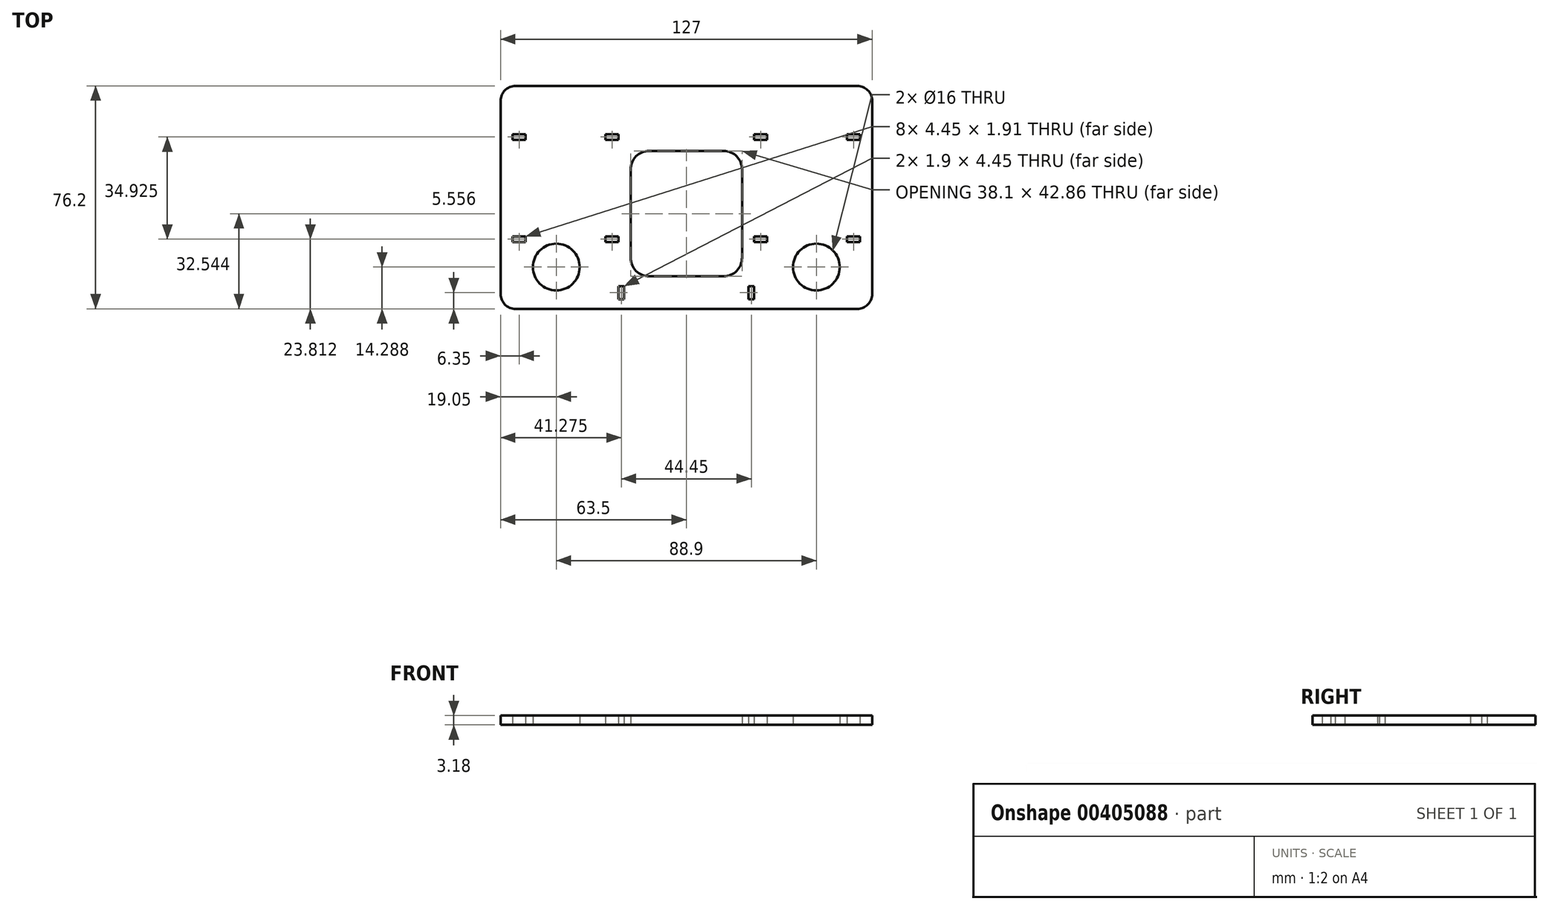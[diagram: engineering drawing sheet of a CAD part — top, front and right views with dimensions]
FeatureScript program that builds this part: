
annotation { "Feature Type Name" : "Feature", "Feature Type Description" : "" }
export const myFeature = defineFeature(function(context is Context, id is Id, definition is map)
    precondition{}
    {
        {
            var Q0;
            Q0=qCreatedBy(makeId("Top.planeOp"),FACE);
            var sketch = newSketch(context, id + "F0", { "sketchPlane" : qUnion([Q0])});
            skLineSegment(sketch, "E0.bottom", {"start": v(63.5, 31.75) * mm, "end": v(-63.5, 31.75) * mm, "construction": true});
            skLineSegment(sketch, "E0.top", {"start": v(63.5, -31.75) * mm, "end": v(-63.5, -31.75) * mm});
            skLineSegment(sketch, "E0.left", {"start": v(63.5, 31.75) * mm, "end": v(63.5, -31.75) * mm});
            skLineSegment(sketch, "E0.right", {"start": v(-63.5, 31.75) * mm, "end": v(-63.5, -31.75) * mm});
            skLineSegment(sketch, "E1.bottom", {"start": v(-19.05, 22.23) * mm, "end": v(19.05, 22.23) * mm});
            skLineSegment(sketch, "E1.top", {"start": v(-19.05, -20.64) * mm, "end": v(19.05, -20.64) * mm});
            skLineSegment(sketch, "E1.left", {"start": v(-19.05, 22.23) * mm, "end": v(-19.05, -20.64) * mm});
            skLineSegment(sketch, "E1.right", {"start": v(19.05, 22.23) * mm, "end": v(19.05, -20.64) * mm});
            skPoint(sketch, "E1.middle", {"position": v(0, 0.8) * mm});
            skLineSegment(sketch, "E2", {"start": v(-63.5, 0) * mm, "end": v(0, 0) * mm, "construction": true});
            skLineSegment(sketch, "E3", {"start": v(0, 0) * mm, "end": v(0, 31.75) * mm, "construction": true});
            skCircle(sketch, "E4", {"center": v(44.45, -17.46) * mm, "radius": 8 * mm});
            skLineSegment(sketch, "E5", {"start": v(19.05, -3.17) * mm, "end": v(63.5, -3.17) * mm, "construction": true});
            skLineSegment(sketch, "E6", {"start": v(44.45, -3.17) * mm, "end": v(44.45, -31.75) * mm, "construction": true});
            skCircle(sketch, "E7.MirrorC", {"center": v(-44.45, -17.46) * mm, "radius": 8 * mm});
            skLineSegment(sketch, "E8.bottom", {"start": v(-59.37, 27.94) * mm, "end": v(-54.93, 27.94) * mm});
            skLineSegment(sketch, "E8.top", {"start": v(-59.37, 26.04) * mm, "end": v(-54.93, 26.04) * mm});
            skLineSegment(sketch, "E8.left", {"start": v(-59.37, 27.94) * mm, "end": v(-59.37, 26.04) * mm});
            skLineSegment(sketch, "E8.right", {"start": v(-54.93, 27.94) * mm, "end": v(-54.93, 26.04) * mm});
            skPoint(sketch, "E8.middle", {"position": v(-57.15, 26.99) * mm});
            skArc(sketch, "E9", {"start": v(-57.15, 31.75) * mm, "mid": v(-61.64, 29.9) * mm, "end": v(-63.5, 25.4) * mm, "construction": true});
            skLineSegment(sketch, "E10.1.0.0", {"start": v(-27.62, 27.94) * mm, "end": v(-23.18, 27.94) * mm});
            skLineSegment(sketch, "E10.1.0.1", {"start": v(-27.62, 27.94) * mm, "end": v(-27.62, 26.04) * mm});
            skLineSegment(sketch, "E10.1.0.2", {"start": v(-27.62, 26.04) * mm, "end": v(-23.18, 26.04) * mm});
            skLineSegment(sketch, "E10.1.0.3", {"start": v(-23.18, 27.94) * mm, "end": v(-23.18, 26.04) * mm});
            skLineSegment(sketch, "E10.direction1", {"start": v(-59.37, 27.94) * mm, "end": v(-27.62, 27.94) * mm, "construction": true});
            skLineSegment(sketch, "E11", {"start": v(-63.5, 9.53) * mm, "end": v(-19.05, 9.53) * mm, "construction": true});
            skLineSegment(sketch, "E12.MirrorCS", {"start": v(-59.37, -6.99) * mm, "end": v(-54.93, -6.99) * mm});
            skLineSegment(sketch, "E13.MirrorCS", {"start": v(-54.93, -8.89) * mm, "end": v(-54.93, -6.99) * mm});
            skLineSegment(sketch, "E14.MirrorCS", {"start": v(-59.37, -8.89) * mm, "end": v(-54.93, -8.89) * mm});
            skPoint(sketch, "E15.MirrorP", {"position": v(-57.15, -7.94) * mm});
            skLineSegment(sketch, "E16.MirrorCS", {"start": v(-59.37, -8.89) * mm, "end": v(-59.37, -6.99) * mm});
            skLineSegment(sketch, "E17.MirrorCS", {"start": v(-27.62, -8.89) * mm, "end": v(-23.18, -8.89) * mm});
            skLineSegment(sketch, "E18.MirrorCS", {"start": v(-27.62, -6.99) * mm, "end": v(-23.18, -6.99) * mm});
            skLineSegment(sketch, "E19.MirrorCS", {"start": v(-27.62, -8.89) * mm, "end": v(-27.62, -6.99) * mm});
            skLineSegment(sketch, "E20.MirrorCS", {"start": v(-23.18, -8.89) * mm, "end": v(-23.18, -6.99) * mm});
            skLineSegment(sketch, "E21.MirrorCS", {"start": v(59.37, 27.94) * mm, "end": v(54.93, 27.94) * mm});
            skLineSegment(sketch, "E22.MirrorCS", {"start": v(59.37, 27.94) * mm, "end": v(59.37, 26.04) * mm});
            skLineSegment(sketch, "E23.MirrorCS", {"start": v(59.37, 26.04) * mm, "end": v(54.93, 26.04) * mm});
            skLineSegment(sketch, "E24.MirrorCS", {"start": v(54.93, 27.94) * mm, "end": v(54.93, 26.04) * mm});
            skLineSegment(sketch, "E25.MirrorCS", {"start": v(27.62, 26.04) * mm, "end": v(23.18, 26.04) * mm});
            skLineSegment(sketch, "E26.MirrorCS", {"start": v(27.62, 27.94) * mm, "end": v(27.62, 26.04) * mm});
            skLineSegment(sketch, "E27.MirrorCS", {"start": v(23.18, 27.94) * mm, "end": v(23.18, 26.04) * mm});
            skLineSegment(sketch, "E28.MirrorCS", {"start": v(27.62, 27.94) * mm, "end": v(23.18, 27.94) * mm});
            skLineSegment(sketch, "E29.MirrorCS", {"start": v(59.37, -8.89) * mm, "end": v(59.37, -6.99) * mm});
            skLineSegment(sketch, "E30.MirrorCS", {"start": v(59.37, -6.98) * mm, "end": v(54.93, -6.98) * mm});
            skLineSegment(sketch, "E31.MirrorCS", {"start": v(54.93, -8.89) * mm, "end": v(54.93, -6.99) * mm});
            skLineSegment(sketch, "E32.MirrorCS", {"start": v(59.37, -8.89) * mm, "end": v(54.93, -8.89) * mm});
            skLineSegment(sketch, "E33.MirrorCS", {"start": v(27.62, -6.98) * mm, "end": v(23.18, -6.98) * mm});
            skLineSegment(sketch, "E34.MirrorCS", {"start": v(27.62, -8.89) * mm, "end": v(23.18, -8.89) * mm});
            skLineSegment(sketch, "E35.MirrorCS", {"start": v(27.62, -8.89) * mm, "end": v(27.62, -6.99) * mm});
            skLineSegment(sketch, "E36.MirrorCS", {"start": v(23.18, -8.89) * mm, "end": v(23.18, -6.99) * mm});
            skLineSegment(sketch, "E37.bottom", {"start": v(-21.27, -28.42) * mm, "end": v(-23.18, -28.42) * mm});
            skLineSegment(sketch, "E37.top", {"start": v(-21.27, -23.97) * mm, "end": v(-23.18, -23.97) * mm});
            skLineSegment(sketch, "E37.left", {"start": v(-21.27, -28.42) * mm, "end": v(-21.27, -23.97) * mm});
            skLineSegment(sketch, "E37.right", {"start": v(-23.18, -28.42) * mm, "end": v(-23.18, -23.97) * mm});
            skPoint(sketch, "E37.middle", {"position": v(-22.23, -26.2) * mm});
            skLineSegment(sketch, "E38", {"start": v(-19.05, -20.64) * mm, "end": v(-19.05, -31.75) * mm, "construction": true});
            skLineSegment(sketch, "E39", {"start": v(-19.05, -26.2) * mm, "end": v(-22.23, -26.2) * mm, "construction": true});
            skLineSegment(sketch, "E40.MirrorCS", {"start": v(23.18, -28.42) * mm, "end": v(23.18, -23.97) * mm});
            skLineSegment(sketch, "E41.MirrorCS", {"start": v(21.27, -23.97) * mm, "end": v(23.18, -23.97) * mm});
            skLineSegment(sketch, "E42.MirrorCS", {"start": v(21.27, -28.42) * mm, "end": v(21.27, -23.97) * mm});
            skLineSegment(sketch, "E43.MirrorCS", {"start": v(21.27, -28.42) * mm, "end": v(23.18, -28.42) * mm});
            skLineSegment(sketch, "E44", {"start": v(-63.5, 31.75) * mm, "end": v(-63.5, 44.45) * mm});
            skLineSegment(sketch, "E45", {"start": v(-63.5, 44.45) * mm, "end": v(63.5, 44.45) * mm});
            skLineSegment(sketch, "E46", {"start": v(63.5, 44.45) * mm, "end": v(63.5, 31.75) * mm});
            skSolve(sketch);
        }
        {
            var Q0;
            Q0 = qSketchRegion(id + "F0", true);
            extrude(context, id + "F1", {"entities" : qUnion([Q0]), "depth" : 3.17 * mm, "offsetDistance" : 25.4 * mm});
        }
        {
            var Q0;
            Q0=makeQuery(id+"F1.opExtrude","SWEPT_EDGE",EDGE,{"disambiguationData":[OSD([sQuery(id+"F0.wireOp",EDGE,"E1.bottom"),sQuery(id+"F0.wireOp",EDGE,"E1.left")])]});
            var Q1;
            Q1=makeQuery(id+"F1.opExtrude","SWEPT_EDGE",EDGE,{"disambiguationData":[OSD([sQuery(id+"F0.wireOp",EDGE,"E1.bottom"),sQuery(id+"F0.wireOp",EDGE,"E1.right")])]});
            var Q2;
            Q2=makeQuery(id+"F1.opExtrude","SWEPT_EDGE",EDGE,{"disambiguationData":[OSD([sQuery(id+"F0.wireOp",EDGE,"E1.top"),sQuery(id+"F0.wireOp",EDGE,"E1.left")])]});
            var Q3;
            Q3=makeQuery(id+"F1.opExtrude","SWEPT_EDGE",EDGE,{"disambiguationData":[OSD([sQuery(id+"F0.wireOp",EDGE,"E1.top"),sQuery(id+"F0.wireOp",EDGE,"E1.right")])]});
            fillet(context, id + "F2", {"entities" : qUnion([Q0, Q1, Q2, Q3]), "radius" : 6.35 * mm, "tangentPropagation" : true, "allowEdgeOverflow" : false});
        }
        {
            var Q0;
            Q0=makeQuery(id+"F1.opExtrude","SWEPT_EDGE",EDGE,{"disambiguationData":[OSD([sQuery(id+"F0.wireOp",EDGE,"E44"),sQuery(id+"F0.wireOp",EDGE,"E45")])]});
            var Q1;
            Q1=makeQuery(id+"F1.opExtrude","SWEPT_EDGE",EDGE,{"disambiguationData":[OSD([sQuery(id+"F0.wireOp",EDGE,"E0.top"),sQuery(id+"F0.wireOp",EDGE,"E0.right")])]});
            var Q2;
            Q2=makeQuery(id+"F1.opExtrude","SWEPT_EDGE",EDGE,{"disambiguationData":[OSD([sQuery(id+"F0.wireOp",EDGE,"E0.top"),sQuery(id+"F0.wireOp",EDGE,"E0.left")])]});
            var Q3;
            Q3=makeQuery(id+"F1.opExtrude","SWEPT_EDGE",EDGE,{"disambiguationData":[OSD([sQuery(id+"F0.wireOp",EDGE,"E45"),sQuery(id+"F0.wireOp",EDGE,"E46")])]});
            fillet(context, id + "F3", {"entities" : qUnion([Q0, Q1, Q2, Q3]), "radius" : 5.08 * mm, "tangentPropagation" : true, "allowEdgeOverflow" : false});
        }
    });
